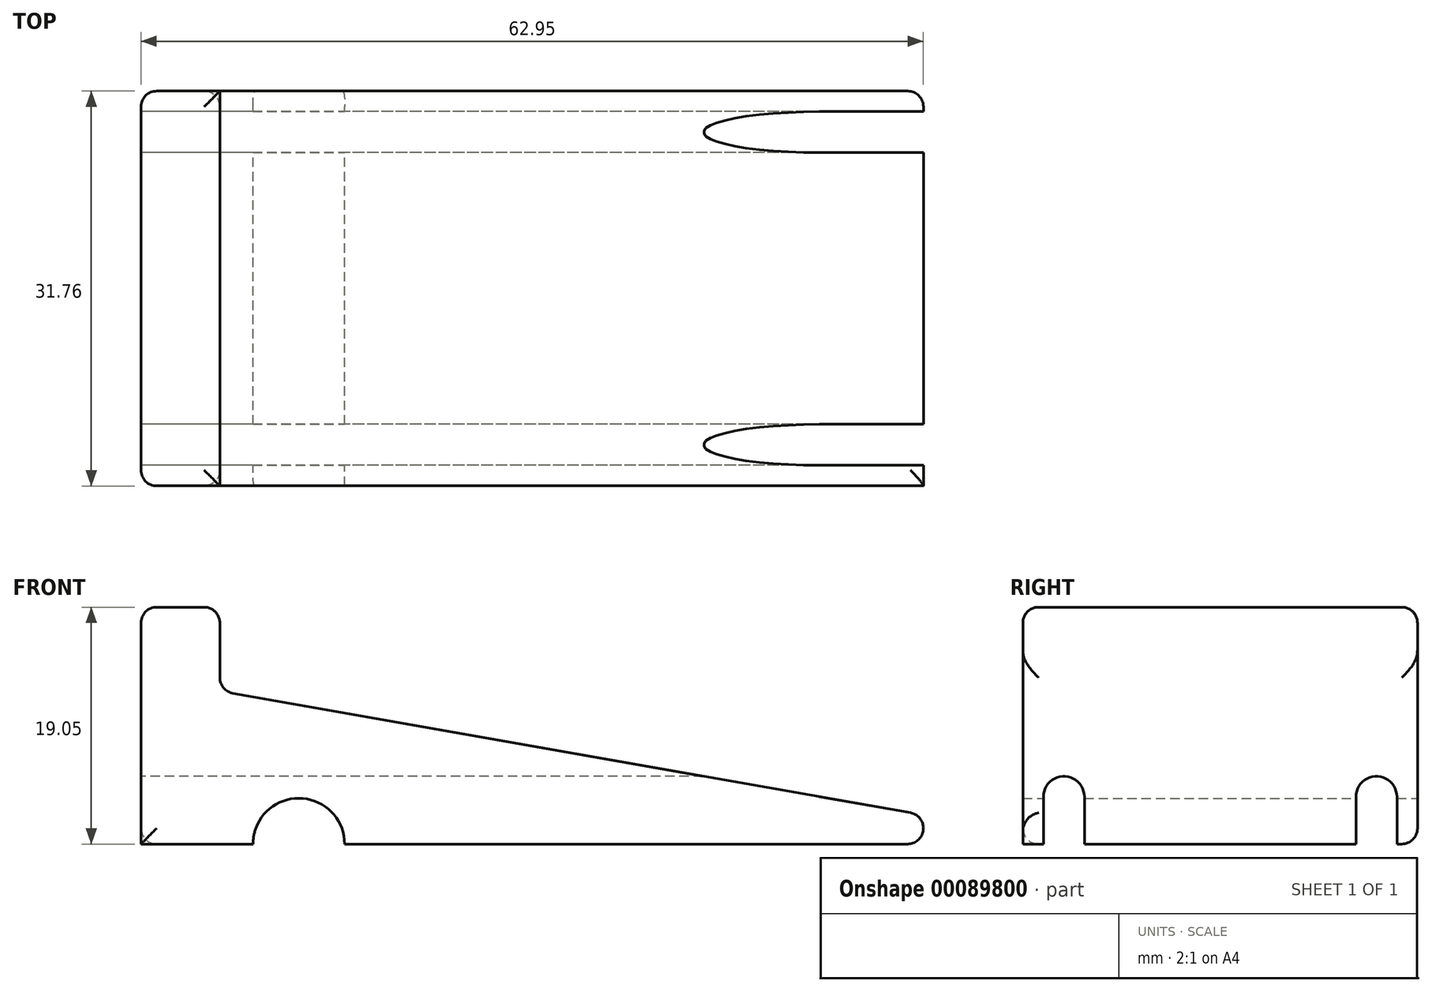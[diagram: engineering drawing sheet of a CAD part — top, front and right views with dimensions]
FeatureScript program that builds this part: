
annotation { "Feature Type Name" : "Feature", "Feature Type Description" : "" }
export const myFeature = defineFeature(function(context is Context, id is Id, definition is map)
    precondition{}
    {
        {
            var Q0;
            Q0=qCreatedBy(makeId("Front.planeOp"),FACE);
            var sketch = newSketch(context, id + "F0", { "sketchPlane" : qUnion([Q0])});
            skLineSegment(sketch, "E0", {"start": v(-38.1, 0) * mm, "end": v(38.1, 0) * mm});
            skLineSegment(sketch, "E1", {"start": v(0, 0) * mm, "end": v(0, 99.15) * mm, "construction": true});
            skLineSegment(sketch, "E2", {"start": v(-38.1, 0) * mm, "end": v(-38.1, 19.05) * mm});
            skLineSegment(sketch, "E3", {"start": v(-38.1, 19.05) * mm, "end": v(-31.75, 19.05) * mm});
            skLineSegment(sketch, "E4", {"start": v(-31.75, 19.05) * mm, "end": v(-31.75, 12.32) * mm});
            skLineSegment(sketch, "E5", {"start": v(-31.75, 12.32) * mm, "end": v(38.1, 0) * mm});
            skSolve(sketch);
        }
        {
            var Q0;
            Q0 = qSketchRegion(id + "F0", true);
            extrude(context, id + "F1", {"entities" : qUnion([Q0]), "endBound" : BoundingType.SYMMETRIC, "depth" : 31.75 * mm});
        }
        {
            var Q0;
            Q0=makeQuery(id+"F1.opExtrude","SWEPT_FACE",FACE,{"disambiguationData":[OSD([sQuery(id+"F0.wireOp",EDGE,"E2")])]});
            var sketch = newSketch(context, id + "F2", { "sketchPlane" : qUnion([Q0])});
            skLineSegment(sketch, "E6", {"start": v(0, 19.05) * mm, "end": v(0, 0) * mm, "construction": true});
            skArc(sketch, "E7", {"start": v(-10.92, 3.81) * mm, "mid": v(-12.57, 5.46) * mm, "end": v(-14.22, 3.8) * mm});
            skLineSegment(sketch, "E8", {"start": v(-15.88, 0) * mm, "end": v(15.88, 0) * mm, "construction": true});
            skLineSegment(sketch, "E9", {"start": v(-14.22, 0) * mm, "end": v(-10.92, 0) * mm});
            skLineSegment(sketch, "E10", {"start": v(-14.22, 3.8) * mm, "end": v(-14.22, 0) * mm});
            skLineSegment(sketch, "E11", {"start": v(-10.92, 3.81) * mm, "end": v(-10.92, 0) * mm});
            skLineSegment(sketch, "E12.MirrorCS", {"start": v(14.22, 3.81) * mm, "end": v(14.22, 0) * mm});
            skLineSegment(sketch, "E13.MirrorCS", {"start": v(14.22, 0) * mm, "end": v(10.92, 0) * mm});
            skArc(sketch, "E14.MirrorCS", {"start": v(10.92, 3.81) * mm, "mid": v(12.57, 5.46) * mm, "end": v(14.22, 3.81) * mm});
            skLineSegment(sketch, "E15.MirrorCS", {"start": v(10.92, 3.81) * mm, "end": v(10.92, 0) * mm});
            skSolve(sketch);
        }
        {
            var Q0;
            Q0 = qSketchRegion(id + "F2", true);
            extrude(context, id + "F3", {"entities" : qUnion([Q0]), "operationType" : NewBodyOperationType.REMOVE, "endBound" : BoundingType.THROUGH_ALL, "oppositeDirection" : true, "depth" : 25.4 * mm});
        }
        {
            var Q0;
            Q0=makeQuery(id+"F1.opExtrude","CAP_FACE",FACE,{"disambiguationData":[OSD([sQuery(id+"F0.wireOp",EDGE,"E0"),sQuery(id+"F0.wireOp",EDGE,"E2"),sQuery(id+"F0.wireOp",EDGE,"E3"),sQuery(id+"F0.wireOp",EDGE,"E4"),sQuery(id+"F0.wireOp",EDGE,"E5")])],"isStart":true});
            var sketch = newSketch(context, id + "F4", { "sketchPlane" : qUnion([Q0])});
            skLineSegment(sketch, "E16", {"start": v(-38.1, 0) * mm, "end": v(38.1, 0) * mm});
            skArc(sketch, "E17", {"start": v(29.08, 0) * mm, "mid": v(25.4, 3.68) * mm, "end": v(21.72, 0) * mm});
            skSolve(sketch);
        }
        {
            var Q0;
            Q0 = qSketchRegion(id + "F4", true);
            extrude(context, id + "F5", {"entities" : qUnion([Q0]), "operationType" : NewBodyOperationType.REMOVE, "endBound" : BoundingType.THROUGH_ALL, "oppositeDirection" : true, "depth" : 25.4 * mm});
        }
        {
            var Q0;
            {var subQ0=sQuery(id+"F0.wireOp",EDGE,"E0");var subQ1=sQuery(id+"F0.wireOp",EDGE,"E5");Q0=makeQuery(id+"F3.boolean.opBoolean","SPLIT",EDGE,{"disambiguationData":[TD([makeQuery(id+"F3.opExtrude","SWEPT_FACE",FACE,{"disambiguationData":[OSD([sQuery(id+"F2.wireOp",EDGE,"E11")])]})])],"derivedFrom":makeQuery(id+"F1.opExtrude","SWEPT_EDGE",EDGE,{"disambiguationData":[OSD([subQ0,subQ1])]})});}
            var Q1;
            {var subQ0=sQuery(id+"F0.wireOp",EDGE,"E0");var subQ1=sQuery(id+"F0.wireOp",EDGE,"E5");Q1=makeQuery(id+"F3.boolean.opBoolean","SPLIT",EDGE,{"disambiguationData":[TD([makeQuery(id+"F3.opExtrude","SWEPT_FACE",FACE,{"disambiguationData":[OSD([sQuery(id+"F2.wireOp",EDGE,"E10")])]})])],"derivedFrom":makeQuery(id+"F1.opExtrude","SWEPT_EDGE",EDGE,{"disambiguationData":[OSD([subQ0,subQ1])]})});}
            var Q2;
            {var subQ0=sQuery(id+"F0.wireOp",EDGE,"E0");var subQ1=sQuery(id+"F0.wireOp",EDGE,"E5");Q2=makeQuery(id+"F3.boolean.opBoolean","SPLIT",EDGE,{"disambiguationData":[TD([makeQuery(id+"F3.opExtrude","SWEPT_FACE",FACE,{"disambiguationData":[OSD([sQuery(id+"F2.wireOp",EDGE,"E12.MirrorCS")])]})])],"derivedFrom":makeQuery(id+"F1.opExtrude","SWEPT_EDGE",EDGE,{"disambiguationData":[OSD([subQ0,subQ1])]})});}
            var Q3;
            Q3=makeQuery(id+"F1.opExtrude","SWEPT_EDGE",EDGE,{"disambiguationData":[OSD([sQuery(id+"F0.wireOp",EDGE,"E4"),sQuery(id+"F0.wireOp",EDGE,"E5")])]});
            var Q4;
            Q4=makeQuery(id+"F1.opExtrude","SWEPT_EDGE",EDGE,{"disambiguationData":[OSD([sQuery(id+"F0.wireOp",EDGE,"E3"),sQuery(id+"F0.wireOp",EDGE,"E4")])]});
            var Q5;
            Q5=makeQuery(id+"F1.opExtrude","SWEPT_EDGE",EDGE,{"disambiguationData":[OSD([sQuery(id+"F0.wireOp",EDGE,"E2"),sQuery(id+"F0.wireOp",EDGE,"E3")])]});
            var Q6;
            {var subQ0=sQuery(id+"F0.wireOp",EDGE,"E0");var subQ1=sQuery(id+"F0.wireOp",EDGE,"E2");Q6=makeQuery(id+"F3.boolean.opBoolean","SPLIT",EDGE,{"disambiguationData":[TD([makeQuery(id+"F3.opExtrude","SWEPT_FACE",FACE,{"disambiguationData":[OSD([sQuery(id+"F2.wireOp",EDGE,"E10")])]})])],"derivedFrom":makeQuery(id+"F1.opExtrude","SWEPT_EDGE",EDGE,{"disambiguationData":[OSD([subQ0,subQ1])]})});}
            var Q7;
            {var subQ0=sQuery(id+"F0.wireOp",EDGE,"E0");var subQ1=sQuery(id+"F0.wireOp",EDGE,"E2");Q7=makeQuery(id+"F3.boolean.opBoolean","SPLIT",EDGE,{"disambiguationData":[TD([makeQuery(id+"F3.opExtrude","SWEPT_FACE",FACE,{"disambiguationData":[OSD([sQuery(id+"F2.wireOp",EDGE,"E11")])]})])],"derivedFrom":makeQuery(id+"F1.opExtrude","SWEPT_EDGE",EDGE,{"disambiguationData":[OSD([subQ0,subQ1])]})});}
            var Q8;
            {var subQ0=sQuery(id+"F0.wireOp",EDGE,"E0");var subQ1=sQuery(id+"F0.wireOp",EDGE,"E2");Q8=makeQuery(id+"F5.boolean.opBoolean","SPLIT",EDGE,{"disambiguationData":[TD([makeQuery(id+"F1.opExtrude","SWEPT_FACE",FACE,{"disambiguationData":[OSD([subQ1])]})])],"derivedFrom":makeQuery(id+"F1.opExtrude","CAP_EDGE",EDGE,{"disambiguationData":[OSD([subQ0])],"isStart":false})});}
            var Q9;
            {var subQ0=sQuery(id+"F0.wireOp",EDGE,"E0");var subQ1=sQuery(id+"F0.wireOp",EDGE,"E5");Q9=makeQuery(id+"F5.boolean.opBoolean","SPLIT",EDGE,{"disambiguationData":[TD([makeQuery(id+"F1.opExtrude","SWEPT_FACE",FACE,{"disambiguationData":[OSD([subQ1])]})])],"derivedFrom":makeQuery(id+"F1.opExtrude","CAP_EDGE",EDGE,{"disambiguationData":[OSD([subQ0])],"isStart":true})});}
            var Q10;
            {var subQ0=sQuery(id+"F0.wireOp",EDGE,"E0");var subQ1=sQuery(id+"F0.wireOp",EDGE,"E2");Q10=makeQuery(id+"F5.boolean.opBoolean","SPLIT",EDGE,{"disambiguationData":[TD([makeQuery(id+"F1.opExtrude","SWEPT_FACE",FACE,{"disambiguationData":[OSD([subQ1])]})])],"derivedFrom":makeQuery(id+"F1.opExtrude","CAP_EDGE",EDGE,{"disambiguationData":[OSD([subQ0])],"isStart":true})});}
            var Q11;
            Q11=makeQuery(id+"F1.opExtrude","CAP_EDGE",EDGE,{"disambiguationData":[OSD([sQuery(id+"F0.wireOp",EDGE,"E5")])],"isStart":false});
            var Q12;
            Q12=makeQuery(id+"F1.opExtrude","CAP_EDGE",EDGE,{"disambiguationData":[OSD([sQuery(id+"F0.wireOp",EDGE,"E2")])],"isStart":false});
            var Q13;
            Q13=makeQuery(id+"F1.opExtrude","CAP_EDGE",EDGE,{"disambiguationData":[OSD([sQuery(id+"F0.wireOp",EDGE,"E2")])],"isStart":true});
            var Q14;
            Q14=makeQuery(id+"F1.opExtrude","CAP_EDGE",EDGE,{"disambiguationData":[OSD([sQuery(id+"F0.wireOp",EDGE,"E3")])],"isStart":false});
            var Q15;
            Q15=makeQuery(id+"F1.opExtrude","CAP_EDGE",EDGE,{"disambiguationData":[OSD([sQuery(id+"F0.wireOp",EDGE,"E3")])],"isStart":true});
            var Q16;
            Q16=makeQuery(id+"F1.opExtrude","CAP_EDGE",EDGE,{"disambiguationData":[OSD([sQuery(id+"F0.wireOp",EDGE,"E5")])],"isStart":true});
            fillet(context, id + "F6", {"entities" : qUnion([Q0, Q1, Q2, Q3, Q4, Q5, Q6, Q7, Q8, Q9, Q10, Q11, Q12, Q13, Q14, Q15, Q16]), "radius" : 1.27 * mm, "tangentPropagation" : true, "allowEdgeOverflow" : false});
        }
    });
